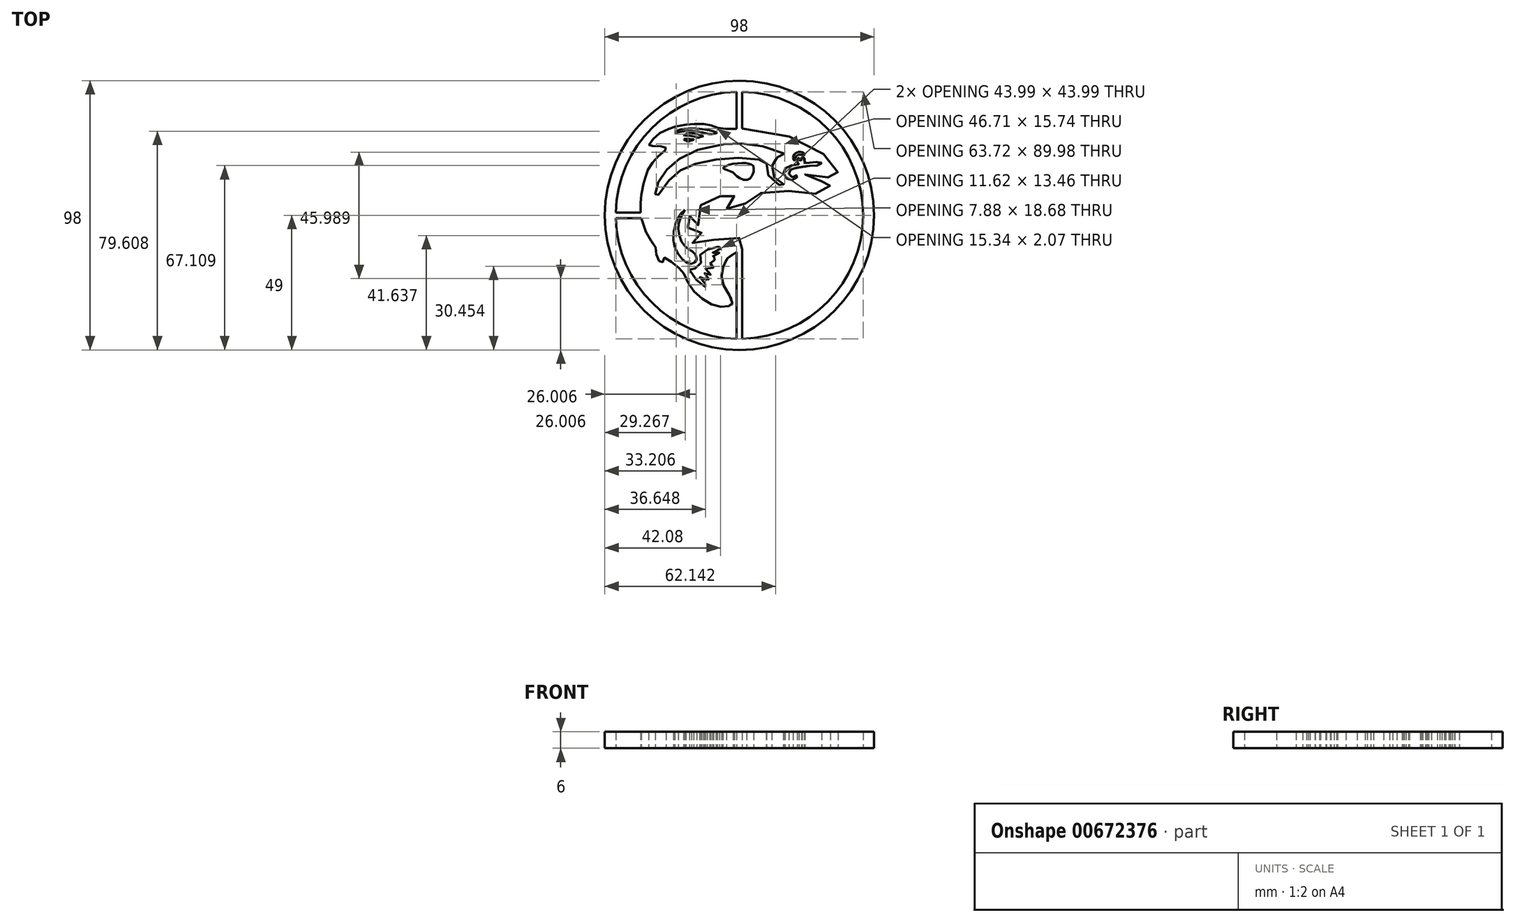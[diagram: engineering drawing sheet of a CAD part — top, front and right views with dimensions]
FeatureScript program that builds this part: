
annotation { "Feature Type Name" : "Feature", "Feature Type Description" : "" }
export const myFeature = defineFeature(function(context is Context, id is Id, definition is map)
    precondition{}
    {
        {
            var Q0;
            Q0=qCreatedBy(makeId("Top.planeOp"),FACE);
            var sketch = newSketch(context, id + "F0", { "sketchPlane" : qUnion([Q0])});
            skFitSpline(sketch, "E0", {"points": [v(9.94, 18.93) * mm, v(9.75, 17.13) * mm, v(10.12, 15.41) * mm, v(11.28, 13.47) * mm, v(13.45, 11.66) * mm, v(15.21, 10.74) * mm, v(16.33, 10.6) * mm, v(16.56, 10.74) * mm, v(16.56, 10.97) * mm, v(16, 11.39) * mm, v(14.84, 12.08) * mm, v(13.27, 13.14) * mm, v(12.34, 14.44) * mm, v(11.89, 16.1) * mm, v(11.9, 17.75) * mm, v(12.16, 19.3) * mm, v(12.76, 20.26) * mm, v(13.54, 20.97) * mm, v(15.05, 21.65) * mm, v(15.87, 21.98) * mm, v(16.3, 22.26) * mm, v(16.34, 22.48) * mm, v(16.09, 22.83) * mm, v(8.22, 25.26) * mm, v(2.24, 26.04) * mm, v(-1.05, 26.14) * mm, v(-4.88, 26) * mm, v(-12.36, 24.66) * mm, v(-19.52, 21.94) * mm, v(-22.17, 20.4) * mm, v(-24.54, 18.57) * mm, v(-27.08, 15.82) * mm, v(-28.66, 13.6) * mm, v(-29.92, 11.2) * mm, v(-30.46, 9.56) * mm, v(-30.64, 8.13) * mm, v(-30.43, 6.42) * mm, v(-30.18, 5.74) * mm, v(-30, 6.2) * mm, v(-28.17, 9.96) * mm, v(-26.2, 12.25) * mm, v(-23.47, 14.9) * mm, v(-22.14, 15.9) * mm, v(-18.96, 17.69) * mm, v(-16.3, 18.65) * mm, v(-11.15, 19.77) * mm, v(-6.64, 20.52) * mm, v(-0.27, 20.96) * mm, v(4.63, 20.6) * mm, v(8.71, 20.11) * mm, v(9.43, 19.86) * mm, v(9.82, 19.58) * mm, v(9.94, 18.93) * mm]});
            skFitSpline(sketch, "E1", {"points": [v(0.97, 19) * mm, v(2.58, 18.93) * mm, v(3.7, 18.72) * mm, v(4.48, 18.5) * mm, v(5.12, 17.93) * mm, v(5.23, 16.97) * mm, v(4.97, 15.29) * mm, v(3.97, 13.57) * mm, v(2.86, 12.89) * mm, v(1.03, 13.1) * mm, v(-0.75, 14.06) * mm, v(-1.36, 14.53) * mm, v(-2.08, 15.46) * mm, v(-2.86, 15.88) * mm, v(-4.58, 16.53) * mm, v(-5.65, 16.92) * mm, v(-5.94, 17.24) * mm, v(-5.47, 17.63) * mm, v(-4.04, 18.35) * mm, v(-1.68, 18.85) * mm, v(0.97, 19) * mm]});
            skFitSpline(sketch, "E2", {"points": [v(21.41, 22.02) * mm, v(22.3, 22.1) * mm, v(23.2, 21.92) * mm, v(23.52, 21.87) * mm, v(23.72, 21.99) * mm, v(23.79, 22.15) * mm, v(23.7, 22.41) * mm, v(23.36, 22.71) * mm, v(22.8, 22.93) * mm, v(21.9, 23.07) * mm, v(21.02, 22.91) * mm, v(20.26, 22.43) * mm, v(19.73, 21.74) * mm, v(19.56, 20.85) * mm, v(19.75, 20.2) * mm, v(19.91, 20.02) * mm, v(20.04, 19.94) * mm, v(20.18, 20) * mm, v(20.27, 20.24) * mm, v(20.4, 20.92) * mm, v(20.87, 21.63) * mm, v(21.41, 22.02) * mm]});
            skFitSpline(sketch, "E3", {"points": [v(21.5, 20.93) * mm, v(21.3, 20.75) * mm, v(21.1, 20.35) * mm, v(21.05, 19.84) * mm, v(21.24, 19.35) * mm, v(21.63, 18.92) * mm, v(21.7, 18.76) * mm, v(21.69, 18.6) * mm, v(21.04, 18.46) * mm, v(19.58, 18.25) * mm, v(18.08, 17.83) * mm, v(16.98, 17.26) * mm, v(16.47, 16.86) * mm, v(16.13, 16.3) * mm, v(16.05, 15.47) * mm, v(16.23, 14.75) * mm, v(16.85, 13.8) * mm, v(17.6, 13.17) * mm, v(18.4, 12.84) * mm, v(19.43, 12.81) * mm, v(20.47, 13.3) * mm, v(20.92, 13.77) * mm, v(21.08, 14.15) * mm, v(21.07, 14.54) * mm, v(20.99, 14.73) * mm, v(20.9, 14.7) * mm, v(20.66, 14.35) * mm, v(20.18, 14) * mm, v(19.7, 13.88) * mm, v(18.85, 13.92) * mm, v(18.32, 14.28) * mm, v(17.98, 15.01) * mm, v(18.05, 15.75) * mm, v(18.25, 16.15) * mm, v(18.68, 16.57) * mm, v(19.36, 16.87) * mm, v(20.66, 17.25) * mm, v(24.88, 17.9) * mm, v(27.22, 18.05) * mm, v(28.25, 18.15) * mm, v(28.93, 18.35) * mm, v(29.46, 18.6) * mm, v(29.82, 18.93) * mm, v(29.92, 19.13) * mm, v(29.89, 19.3) * mm, v(29.62, 19.38) * mm, v(25.2, 19.2) * mm, v(24.18, 19.05) * mm, v(23.77, 18.99) * mm, v(23.62, 19.03) * mm, v(23.58, 19.2) * mm, v(23.7, 19.5) * mm, v(23.73, 19.9) * mm, v(23.71, 20.44) * mm, v(23.56, 20.85) * mm, v(23.3, 21.16) * mm, v(23, 21.25) * mm, v(22.65, 21.22) * mm, v(22.67, 20.96) * mm, v(22.76, 20.84) * mm, v(22.82, 20.5) * mm, v(22.72, 20.19) * mm, v(22.49, 20.02) * mm, v(22.19, 20) * mm, v(21.87, 20.14) * mm, v(21.67, 20.32) * mm, v(21.57, 20.66) * mm, v(21.5, 20.93) * mm]});
            skFitSpline(sketch, "E4", {"points": [v(-20.25, 27.65) * mm, v(-19.5, 27.17) * mm, v(-19.03, 26.97) * mm, v(-18.52, 26.93) * mm, v(-17.93, 27.09) * mm, v(-16.73, 27.52) * mm, v(-16.64, 27.57) * mm, v(-16.64, 27.62) * mm, v(-16.75, 27.64) * mm, v(-17.23, 27.67) * mm, v(-17.9, 27.74) * mm, v(-18.57, 27.8) * mm, v(-19.37, 27.76) * mm, v(-20.25, 27.65) * mm]});
            skFitSpline(sketch, "E5", {"points": [v(-20.38, 29.19) * mm, v(-18.86, 29.08) * mm, v(-17.7, 28.96) * mm, v(-16.58, 28.74) * mm, v(-15.96, 28.56) * mm, v(-15.44, 28.35) * mm, v(-15.27, 28.3) * mm, v(-14.93, 28.28) * mm, v(-14.76, 28.32) * mm, v(-14.3, 28.47) * mm, v(-13.17, 28.76) * mm, v(-13.17, 28.79) * mm, v(-13.62, 28.98) * mm, v(-14.64, 29.33) * mm, v(-15.47, 29.58) * mm, v(-16.28, 29.76) * mm, v(-17.15, 29.84) * mm, v(-18.15, 29.83) * mm, v(-19.04, 29.7) * mm, v(-19.76, 29.46) * mm, v(-20.38, 29.19) * mm]});
            skFitSpline(sketch, "E6", {"points": [v(-23.47, 30.35) * mm, v(-23.52, 30.27) * mm, v(-23.5, 30.18) * mm, v(-23.38, 30.11) * mm, v(-22.06, 30.3) * mm, v(-20.42, 30.55) * mm, v(-18.8, 30.69) * mm, v(-16.61, 30.68) * mm, v(-14.3, 30.4) * mm, v(-12.94, 30.03) * mm, v(-11.47, 29.6) * mm, v(-11.02, 29.52) * mm, v(-10.28, 29.54) * mm, v(-9.04, 29.78) * mm, v(-8.09, 30.06) * mm, v(-8.08, 30.09) * mm, v(-8.4, 30.2) * mm, v(-9.8, 30.64) * mm, v(-11.44, 31.03) * mm, v(-13.51, 31.38) * mm, v(-15.7, 31.6) * mm, v(-16.67, 31.66) * mm, v(-18.07, 31.65) * mm, v(-19.8, 31.5) * mm, v(-21.03, 31.26) * mm, v(-21.94, 31.01) * mm, v(-22.85, 30.69) * mm, v(-23.47, 30.35) * mm]});
            skFitSpline(sketch, "E7", {"points": [v(-19.85, 1.98) * mm, v(-21.43, 0.54) * mm, v(-22.67, -1.35) * mm, v(-23.4, -3.5) * mm, v(-24.06, -7.62) * mm, v(-23.55, -11.46) * mm, v(-22.03, -14.44) * mm, v(-20.5, -16.2) * mm, v(-19.1, -17.24) * mm, v(-17.71, -17.64) * mm, v(-16.8, -17.47) * mm, v(-15.86, -16.72) * mm, v(-15.57, -15.69) * mm, v(-15.97, -14.31) * mm, v(-16.84, -13.33) * mm, v(-17.9, -12.72) * mm, v(-19.07, -11.99) * mm, v(-20.12, -10.96) * mm, v(-21.31, -8.94) * mm, v(-22.11, -6.34) * mm, v(-22.28, -4.1) * mm, v(-21.87, -2.3) * mm, v(-21.31, -0.6) * mm, v(-20.41, 1.1) * mm, v(-19.85, 1.98) * mm]});
            skFitSpline(sketch, "E8", {"points": [v(-18.16, -19.8) * mm, v(-17.32, -21.45) * mm, v(-16.06, -23.12) * mm, v(-14.77, -24.5) * mm, v(-13.25, -25.65) * mm, v(-12.46, -26.05) * mm, v(-12, -26.2) * mm, v(-11.72, -26.18) * mm, v(-11.68, -26.01) * mm, v(-11.96, -25.52) * mm, v(-12.63, -24.75) * mm, v(-13.54, -23.7) * mm, v(-14.13, -22.99) * mm, v(-14.4, -22.6) * mm, v(-14.48, -22.43) * mm, v(-14.45, -22.35) * mm, v(-14.35, -22.33) * mm, v(-13.4, -22.77) * mm, v(-12.08, -23.43) * mm, v(-11.5, -23.67) * mm, v(-11.17, -23.78) * mm, v(-10.95, -23.81) * mm, v(-10.83, -23.78) * mm, v(-10.84, -23.65) * mm, v(-11.2, -23.18) * mm, v(-11.95, -22.37) * mm, v(-12.57, -21.5) * mm, v(-12.68, -21.24) * mm, v(-12.7, -21.13) * mm, v(-12.67, -21.04) * mm, v(-12.58, -21.04) * mm, v(-11.68, -21.47) * mm, v(-11.14, -21.63) * mm, v(-10.63, -21.68) * mm, v(-10.44, -21.56) * mm, v(-10.4, -21.34) * mm, v(-10.56, -21.07) * mm, v(-12.2, -19.57) * mm, v(-12.34, -19.4) * mm, v(-12.3, -19.27) * mm, v(-12.11, -19.21) * mm, v(-10.08, -19.2) * mm, v(-9.68, -19.12) * mm, v(-9.45, -18.99) * mm, v(-9.4, -18.76) * mm, v(-9.54, -18.55) * mm, v(-9.85, -18.2) * mm, v(-10.42, -17.6) * mm, v(-10.61, -17.36) * mm, v(-10.75, -17.07) * mm, v(-10.7, -16.82) * mm, v(-10.4, -16.59) * mm, v(-9.63, -16.32) * mm, v(-8.88, -16.22) * mm, v(-8.67, -16.2) * mm, v(-8.58, -16.12) * mm, v(-8.57, -15.98) * mm, v(-8.57, -15.68) * mm, v(-8.74, -15.48) * mm, v(-9.07, -15.3) * mm, v(-9.6, -15.22) * mm, v(-9.97, -15.17) * mm, v(-10.4, -15.19) * mm, v(-10.43, -15.14) * mm, v(-10.4, -15.1) * mm, v(-8.85, -14.63) * mm, v(-7.78, -14.17) * mm, v(-7.35, -13.9) * mm, v(-7.24, -13.78) * mm, v(-7.23, -13.65) * mm, v(-7.98, -13.64) * mm, v(-8.54, -13.71) * mm, v(-9.18, -13.7) * mm, v(-9.64, -13.66) * mm, v(-9.76, -13.53) * mm, v(-9.71, -13.39) * mm, v(-8, -12.62) * mm, v(-6.85, -12.09) * mm, v(-6.76, -12.01) * mm, v(-6.6, -11.88) * mm, v(-6.5, -11.73) * mm, v(-6.55, -11.54) * mm, v(-6.9, -11.44) * mm, v(-7.38, -11.41) * mm, v(-8.42, -11.56) * mm, v(-9.9, -11.9) * mm, v(-11.47, -12.47) * mm, v(-12.3, -12.88) * mm, v(-13.24, -13.5) * mm, v(-14.1, -14.22) * mm, v(-14.35, -14.47) * mm, v(-14.26, -14.66) * mm, v(-13.98, -15.62) * mm, v(-14, -17) * mm, v(-14.45, -18.23) * mm, v(-15.27, -19.01) * mm, v(-15.86, -19.24) * mm, v(-16.35, -19.33) * mm, v(-17.7, -19.34) * mm, v(-17.88, -19.37) * mm, v(-18.1, -19.46) * mm, v(-18.18, -19.62) * mm, v(-18.16, -19.8) * mm]});
            skFitSpline(sketch, "E9", {"points": [v(-12.31, -31.17) * mm, v(-10.32, -32.28) * mm, v(-8.54, -32.88) * mm, v(-6.97, -33.25) * mm, v(-5.93, -33.27) * mm, v(-4.7, -33.2) * mm, v(-3.24, -32.96) * mm, v(-2.34, -32.67) * mm, v(-2.32, -32.64) * mm, v(-2.46, -32.24) * mm, v(-2.77, -31.31) * mm, v(-3.16, -30.07) * mm, v(-4.29, -28.1) * mm, v(-5.35, -26.25) * mm, v(-6.13, -24.32) * mm, v(-6.39, -22.92) * mm, v(-6.43, -21.56) * mm, v(-6.07, -19.48) * mm, v(-5.48, -17.71) * mm, v(-4.84, -16.4) * mm, v(-3.86, -15.2) * mm, v(-1.97, -13.96) * mm, v(0.68, -12.51) * mm, v(2.1, -11.73) * mm, v(2.42, -11.4) * mm, v(2.66, -11.07) * mm, v(2.66, -10.45) * mm, v(2.4, -9.75) * mm, v(1.95, -9.14) * mm, v(1.38, -8.75) * mm, v(0.1, -8.3) * mm, v(-0.83, -8.16) * mm, v(-1.95, -8.01) * mm, v(-3.88, -8.03) * mm, v(-6.13, -8.2) * mm, v(-8.07, -8.58) * mm, v(-9.62, -9.1) * mm, v(-11.89, -10) * mm, v(-13.4, -10.7) * mm, v(-14.65, -11.09) * mm, v(-15.73, -11) * mm, v(-16.56, -10.54) * mm, v(-17.07, -10.05) * mm, v(-17.32, -9.78) * mm, v(-17.37, -9.6) * mm, v(-17.3, -9.46) * mm, v(-16.96, -9.16) * mm, v(-16.04, -8.54) * mm, v(-15.32, -8.06) * mm, v(-14.78, -7.64) * mm, v(-14.33, -7.12) * mm, v(-14.01, -6.7) * mm, v(-13.82, -6.3) * mm, v(-13.77, -6.13) * mm, v(-13.76, -5.8) * mm, v(-13.81, -5.67) * mm, v(-14.09, -5.43) * mm, v(-14.6, -5.22) * mm, v(-15.52, -5.01) * mm, v(-16.53, -4.86) * mm, v(-17.4, -4.73) * mm, v(-18.55, -4.58) * mm, v(-19.04, -4.36) * mm, v(-19.26, -4.13) * mm, v(-19.45, -3.77) * mm, v(-19.49, -3.13) * mm, v(-19.43, -2.7) * mm, v(-19.24, -1.9) * mm, v(-18.88, -1.03) * mm, v(-18.6, -0.58) * mm, v(-18.46, -0.37) * mm, v(-18.35, -0.3) * mm, v(-18.2, -0.3) * mm, v(-18.05, -0.4) * mm, v(-17.86, -0.73) * mm, v(-17.38, -1.72) * mm, v(-16.9, -2.66) * mm, v(-16.54, -3.2) * mm, v(-16.26, -3.54) * mm, v(-15.96, -3.82) * mm, v(-15.76, -3.95) * mm, v(-15.55, -3.98) * mm, v(-15.3, -3.92) * mm, v(-15.07, -3.63) * mm, v(-14.86, -3.09) * mm, v(-14.7, -2.32) * mm, v(-14.56, -1.44) * mm, v(-14.45, 0) * mm, v(-14.38, 1.85) * mm, v(-14.32, 2.95) * mm, v(-14.16, 3.53) * mm, v(-13.9, 3.94) * mm, v(-13.33, 4.5) * mm, v(-12.42, 5.04) * mm, v(-11.43, 5.55) * mm, v(-10.24, 6.08) * mm, v(-8.94, 6.42) * mm, v(-6.75, 7.02) * mm, v(-5.2, 7.4) * mm, v(-3.84, 7.7) * mm, v(-3.15, 7.8) * mm, v(-2.56, 7.86) * mm, v(-2.2, 7.83) * mm, v(-1.95, 7.74) * mm, v(-1.84, 7.67) * mm, v(-1.78, 7.53) * mm, v(-1.79, 7.27) * mm, v(-1.9, 6.93) * mm, v(-2.17, 6.43) * mm, v(-2.73, 5.55) * mm, v(-3.22, 4.76) * mm, v(-3.7, 4.14) * mm, v(-4.21, 3.58) * mm, v(-4.54, 3.24) * mm, v(-4.72, 3) * mm, v(-4.76, 2.68) * mm, v(-4.7, 2.42) * mm, v(-4.47, 2.24) * mm, v(-4.17, 2.08) * mm, v(-3.84, 2.03) * mm, v(-3.17, 2.13) * mm, v(-2.55, 2.33) * mm, v(-1.8, 2.62) * mm, v(0.61, 3.56) * mm, v(1.9, 4.1) * mm, v(2.7, 4.63) * mm, v(3.37, 5.2) * mm, v(4.28, 6.27) * mm, v(4.96, 7.06) * mm, v(5.57, 7.58) * mm, v(6.43, 7.97) * mm, v(7.22, 8.08) * mm, v(9.12, 8.22) * mm, v(11.69, 8.42) * mm, v(14.75, 8.79) * mm, v(16.32, 8.9) * mm, v(17.14, 8.95) * mm, v(18.37, 8.9) * mm, v(19.57, 8.76) * mm, v(23.48, 8.15) * mm, v(24.83, 8) * mm, v(25.8, 7.94) * mm, v(27.33, 7.9) * mm, v(28.98, 7.93) * mm, v(29.73, 8.05) * mm, v(30.47, 8.27) * mm, v(31.16, 8.6) * mm, v(31.75, 8.97) * mm, v(32.15, 9.32) * mm, v(32.68, 10.12) * mm, v(32.92, 10.69) * mm, v(33.06, 11.26) * mm, v(33.08, 12.15) * mm, v(32.93, 12.63) * mm, v(32.76, 12.9) * mm, v(32.41, 13.13) * mm, v(32.18, 13.17) * mm, v(31.65, 13.08) * mm, v(31.13, 12.88) * mm, v(30.38, 12.62) * mm, v(29.76, 12.46) * mm, v(28.65, 12.46) * mm, v(27.5, 12.74) * mm, v(26.5, 13.11) * mm, v(24.9, 13.85) * mm, v(24.14, 14.3) * mm, v(23.84, 14.58) * mm, v(23.78, 14.72) * mm, v(23.84, 14.83) * mm, v(24.18, 14.97) * mm, v(25.14, 15.08) * mm, v(27.22, 15.1) * mm, v(28.67, 14.92) * mm, v(29.89, 14.65) * mm, v(31.28, 14.17) * mm, v(32.69, 13.6) * mm, v(33.71, 13.17) * mm, v(34.25, 13.03) * mm, v(34.78, 13) * mm, v(35.15, 13.15) * mm, v(35.48, 13.47) * mm, v(35.71, 13.91) * mm, v(35.85, 14.66) * mm, v(35.85, 15.5) * mm, v(35.81, 15.78) * mm, v(35.69, 16.39) * mm, v(35.47, 17.1) * mm, v(34.93, 18.13) * mm, v(34.43, 18.86) * mm, v(33, 20.37) * mm, v(30.7, 22.18) * mm, v(28.11, 23.95) * mm, v(25.14, 25.66) * mm, v(23.46, 26.48) * mm, v(16.75, 29.1) * mm, v(10.13, 30.85) * mm, v(4.85, 31.51) * mm, v(0, 31.54) * mm, v(-3.4, 31.5) * mm, v(-6.58, 31.62) * mm, v(-8, 31.92) * mm, v(-9.34, 32.42) * mm, v(-10.49, 32.78) * mm, v(-12.14, 33.1) * mm, v(-14.01, 33.28) * mm, v(-16.74, 33.28) * mm, v(-18.5, 33.13) * mm, v(-21.94, 32.6) * mm, v(-23.83, 32.15) * mm, v(-25.07, 31.77) * mm, v(-27.86, 30.54) * mm, v(-29.87, 29.24) * mm, v(-31.43, 27.78) * mm, v(-32.3, 26.64) * mm, v(-33.04, 25.4) * mm, v(-33.06, 25.33) * mm, v(-33.06, 25.28) * mm, v(-32.91, 25.27) * mm, v(-30.88, 25.28) * mm, v(-28.97, 25.14) * mm, v(-27.75, 24.95) * mm, v(-27.14, 24.79) * mm, v(-26.8, 24.58) * mm, v(-26.68, 24.46) * mm, v(-26.65, 24.22) * mm, v(-26.7, 24.03) * mm, v(-27.36, 23.35) * mm, v(-29.45, 21.56) * mm, v(-31.14, 19.84) * mm, v(-31.99, 18.73) * mm, v(-33.23, 16.86) * mm, v(-33.53, 15.92) * mm, v(-34.27, 13.72) * mm, v(-34.65, 12.42) * mm, v(-35.25, 10.12) * mm, v(-35.87, 6.7) * mm, v(-36, 5.04) * mm, v(-36, 2.45) * mm, v(-35.77, -0.58) * mm, v(-34.42, -4.96) * mm, v(-33.55, -6.95) * mm, v(-32.45, -8.8) * mm, v(-31.58, -9.93) * mm, v(-30.82, -10.96) * mm, v(-30.5, -11.78) * mm, v(-30.38, -12.66) * mm, v(-30.32, -13.62) * mm, v(-30.05, -14.81) * mm, v(-29.7, -15.78) * mm, v(-29.27, -16.59) * mm, v(-28.94, -17) * mm, v(-28.62, -17.26) * mm, v(-28.36, -17.3) * mm, v(-28.1, -17.22) * mm, v(-27.85, -16.85) * mm, v(-27.7, -16.43) * mm, v(-27.53, -15.86) * mm, v(-27.4, -15.5) * mm, v(-27.29, -15.4) * mm, v(-27.1, -15.36) * mm, v(-26.7, -15.51) * mm, v(-24.94, -16.78) * mm, v(-23.17, -18.23) * mm, v(-22, -19.2) * mm, v(-21.14, -20) * mm, v(-20.6, -20.66) * mm, v(-20.05, -21.6) * mm, v(-19.19, -23.47) * mm, v(-18.3, -25.13) * mm, v(-16.96, -27.1) * mm, v(-16, -28.22) * mm, v(-13.85, -30.13) * mm, v(-12.31, -31.17) * mm]});
            skLineSegment(sketch, "E10.bottom", {"start": v(32.98, 30.62) * mm, "end": v(-32.98, 30.62) * mm, "construction": true});
            skLineSegment(sketch, "E10.top", {"start": v(32.98, -30.62) * mm, "end": v(-32.98, -30.62) * mm, "construction": true});
            skLineSegment(sketch, "E10.left", {"start": v(32.98, 30.62) * mm, "end": v(32.98, -30.62) * mm, "construction": true});
            skLineSegment(sketch, "E10.right", {"start": v(-32.98, 30.62) * mm, "end": v(-32.98, -30.62) * mm, "construction": true});
            skPoint(sketch, "E10.middle", {"position": v(0, 0) * mm});
            skCircle(sketch, "E11", {"center": v(0, 0) * mm, "radius": 49 * mm});
            skCircle(sketch, "E12", {"center": v(0, 0) * mm, "radius": 45 * mm});
            skPoint(sketch, "E13", {"position": v(-35.53, -1.5) * mm});
            skPoint(sketch, "E14", {"position": v(0, 30.62) * mm});
            skPoint(sketch, "E15.MirrorP", {"position": v(2, 30.62) * mm});
            skLineSegment(sketch, "E16", {"start": v(1, 44.99) * mm, "end": v(1, 31.56) * mm});
            skLineSegment(sketch, "E17", {"start": v(-44.99, 1) * mm, "end": v(-35.97, 1) * mm});
            skLineSegment(sketch, "E18.MirrorCS", {"start": v(-44.99, -1) * mm, "end": v(-35.97, -1) * mm});
            skLineSegment(sketch, "E19", {"start": v(-35.97, -1) * mm, "end": v(-35.68, -1) * mm});
            skLineSegment(sketch, "E20", {"start": v(1, -44.99) * mm, "end": v(1, -12.35) * mm});
            skLineSegment(sketch, "E21", {"start": v(-1, -44.99) * mm, "end": v(-1, -13.41) * mm});
            skLineSegment(sketch, "E22", {"start": v(-1, 44.99) * mm, "end": v(-1, 31.52) * mm});
            skSolve(sketch);
        }
        {
            var Q0;
            Q0=makeQuery(id+"F0.imprint","IMPRINT",FACE,{"disambiguationData":[TD([[makeQuery(id+"F0.imprint","IMPRINT",EDGE,{"derivedFrom":sQuery(id+"F0.wireOp",EDGE,"E0")}),-1.0]])]});
            var Q1;
            Q1=makeQuery(id+"F0.imprint","IMPRINT",FACE,{"disambiguationData":[TD([[makeQuery(id+"F0.imprint","IMPRINT",EDGE,{"derivedFrom":sQuery(id+"F0.wireOp",EDGE,"Ee5ypbTY-de8B-Ul5P-N9UB-f2g9svrHJzog.bottom")}),1.0]])]});
            var Q2;
            Q2=makeQuery(id+"F0.imprint","IMPRINT",FACE,{"disambiguationData":[TD([[makeQuery(id+"F0.imprint","IMPRINT",EDGE,{"derivedFrom":sQuery(id+"F0.wireOp",EDGE,"xDsgpKw9-rZTx-TwXe-moTF-xAwrscQXLduq.right")}),-1.0]])]});
            var Q3;
            Q3=makeQuery(id+"F0.imprint","IMPRINT",FACE,{"disambiguationData":[TD([[makeQuery(id+"F0.imprint","IMPRINT",EDGE,{"derivedFrom":sQuery(id+"F0.wireOp",EDGE,"Ee5ypbTY-de8B-Ul5P-N9UB-f2g9svrHJzog.top")}),-1.0]])]});
            var Q4;
            {var subQ0=sQuery(id+"F0.wireOp",EDGE,"E17");Q4=makeQuery(id+"F0.imprint","IMPRINT",FACE,{"disambiguationData":[TD([[makeQuery(id+"F0.imprint","IMPRINT",EDGE,{"derivedFrom":subQ0}),-1.0]])]});}
            var Q5;
            {var subQ0=sQuery(id+"F0.wireOp",EDGE,"E20");Q5=makeQuery(id+"F0.imprint","IMPRINT",FACE,{"disambiguationData":[TD([[makeQuery(id+"F0.imprint","IMPRINT",EDGE,{"derivedFrom":subQ0}),1.0]])]});}
            var Q6;
            Q6=makeQuery(id+"F0.imprint","IMPRINT",FACE,{"disambiguationData":[TD([[makeQuery(id+"F0.imprint","IMPRINT",EDGE,{"derivedFrom":sQuery(id+"F0.wireOp",EDGE,"E11")}),1.0]])]});
            var Q7;
            {var subQ0=sQuery(id+"F0.wireOp",EDGE,"E16");Q7=makeQuery(id+"F0.imprint","IMPRINT",FACE,{"disambiguationData":[TD([[makeQuery(id+"F0.imprint","IMPRINT",EDGE,{"derivedFrom":subQ0}),-1.0]])]});}
            extrude(context, id + "F1", {"entities" : qUnion([Q0, Q1, Q2, Q3, Q4, Q5, Q6, Q7]), "depth" : 6 * mm, "offsetDistance" : 25 * mm});
        }
    });
